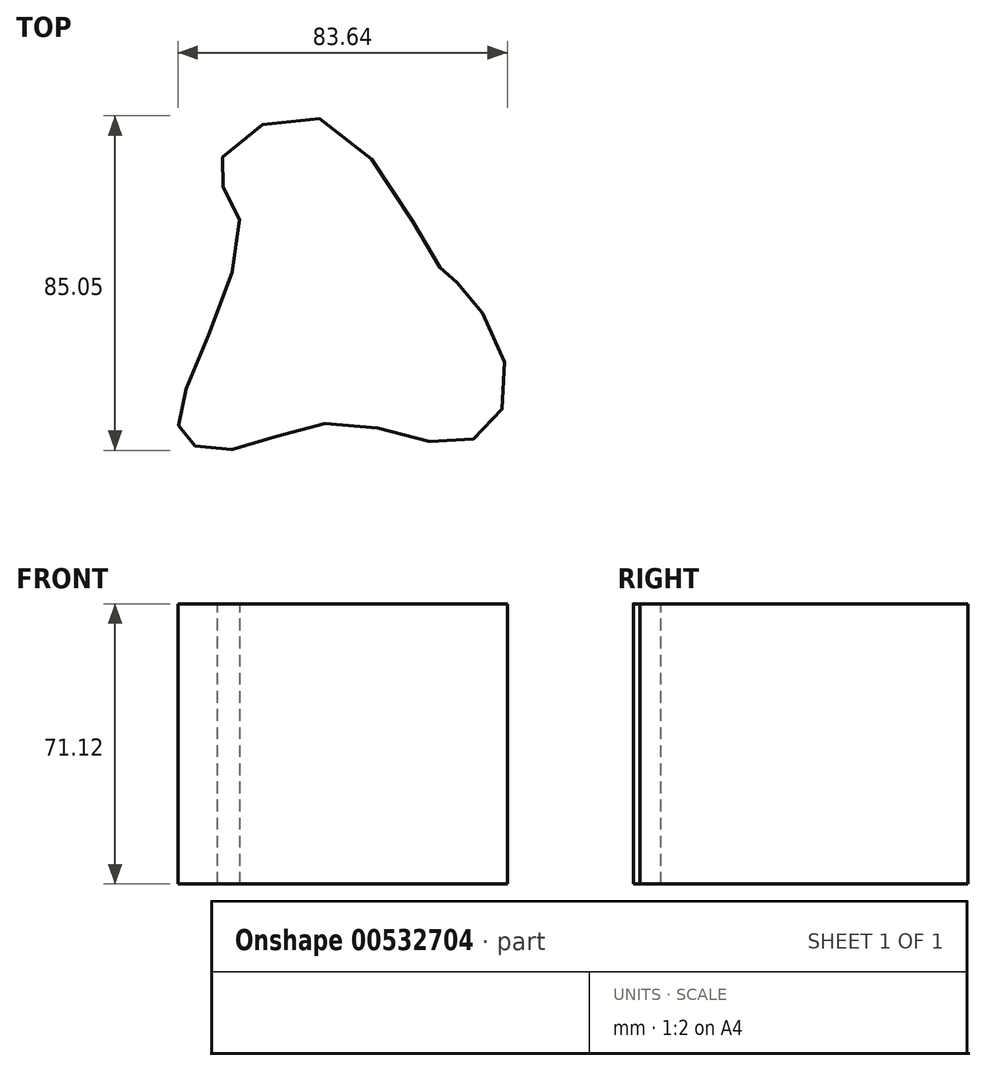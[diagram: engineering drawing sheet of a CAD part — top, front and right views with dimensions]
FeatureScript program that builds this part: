
annotation { "Feature Type Name" : "Feature", "Feature Type Description" : "" }
export const myFeature = defineFeature(function(context is Context, id is Id, definition is map)
    precondition{}
    {
        {
            var Q0;
            Q0=qCreatedBy(makeId("Top.planeOp"),FACE);
            var sketch = newSketch(context, id + "F0", { "sketchPlane" : qUnion([Q0])});
            skFitSpline(sketch, "E0", {"points": [v(30.97, 0) * mm, v(0, 37.98) * mm, v(-25.44, 25.07) * mm, v(-20.1, 13.27) * mm, v(-32.26, -27.65) * mm, v(-34.47, -42.77) * mm, v(-22.12, -46.27) * mm, v(5.72, -39.45) * mm, v(36.69, -44.43) * mm, v(48.12, -28.76) * mm, v(35.95, -4.24) * mm, v(30.97, 0) * mm]});
            skSolve(sketch);
        }
        {
            var Q0;
            Q0=makeQuery(id+"F0.imprint","IMPRINT",FACE,{"disambiguationData":[TD([[makeQuery(id+"F0.imprint","IMPRINT",EDGE,{"derivedFrom":sQuery(id+"F0.wireOp",EDGE,"E0")}),1.0]])]});
            extrude(context, id + "F1", {"entities" : qUnion([Q0]), "depth" : 25.4 * mm, "offsetDistance" : 25.4 * mm});
        }
        {
            var Q0;
            Q0=makeQuery(id+"F1.opExtrude","CAP_FACE",FACE,{"disambiguationData":[OSD([sQuery(id+"F0.wireOp",EDGE,"E0")])],"isStart":false});
            extrude(context, id + "F2", {"entities" : qUnion([Q0]), "operationType" : NewBodyOperationType.ADD, "depth" : 45.72 * mm, "offsetDistance" : 25.4 * mm});
        }
    });
